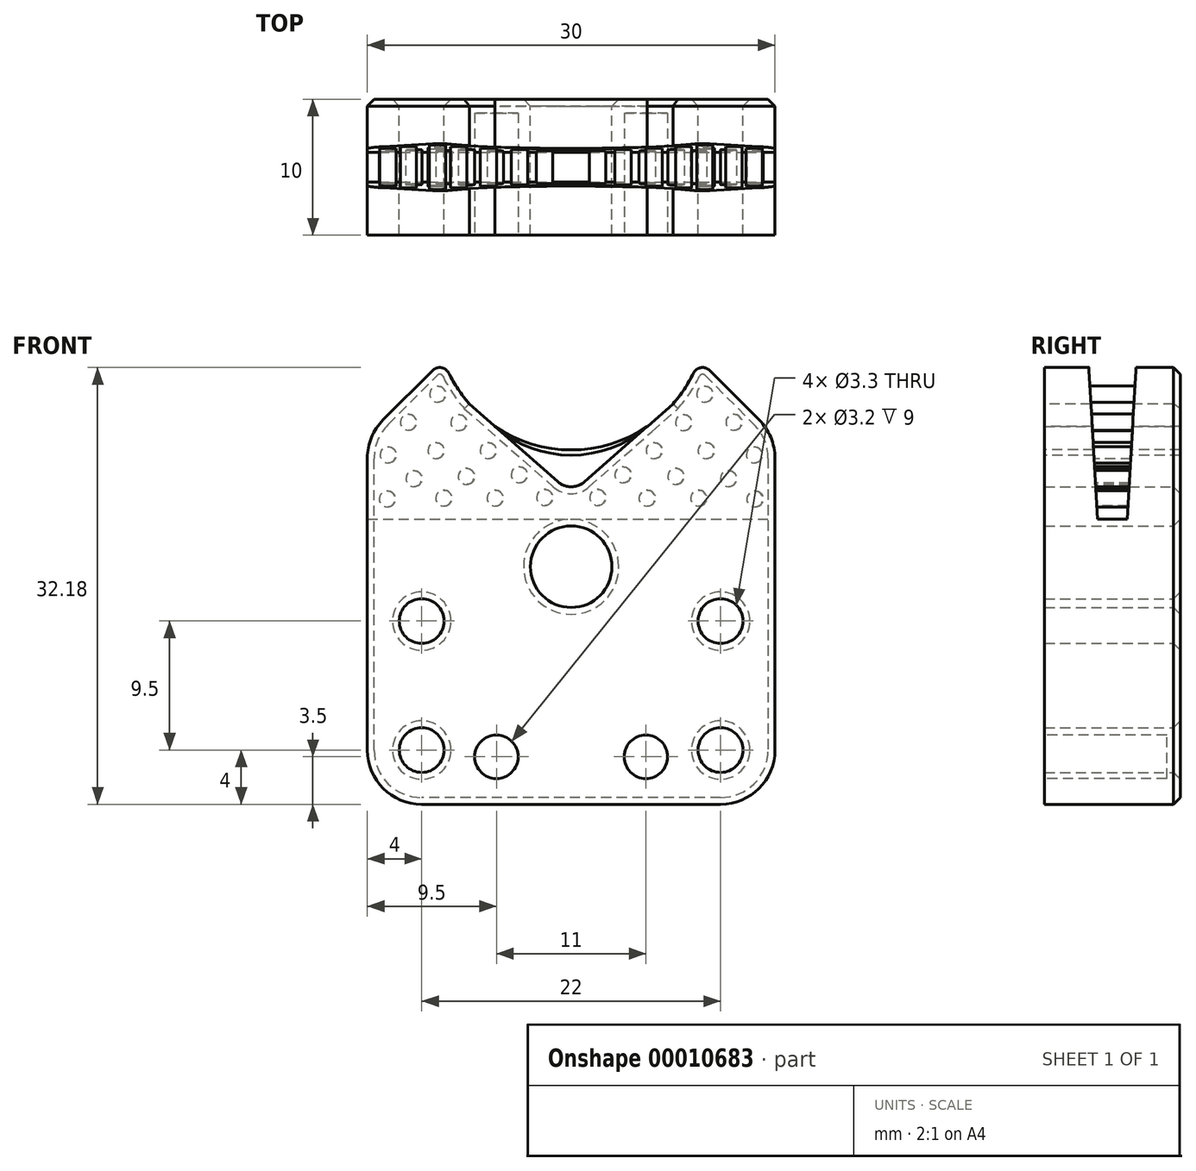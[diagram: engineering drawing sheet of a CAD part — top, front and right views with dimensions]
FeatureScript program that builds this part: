
annotation { "Feature Type Name" : "Feature", "Feature Type Description" : "" }
export const myFeature = defineFeature(function(context is Context, id is Id, definition is map)
    precondition{}
    {
        {
            var Q0;
            Q0=qCreatedBy(makeId("Front.planeOp"),FACE);
            var sketch = newSketch(context, id + "F0", { "sketchPlane" : qUnion([Q0])});
            skLineSegment(sketch, "E0.rect.bottom", {"start": v(15, -19.5) * mm, "end": v(-15, -19.5) * mm});
            skLineSegment(sketch, "E0.rect.top", {"start": v(15, 10) * mm, "end": v(-15, 10) * mm});
            skLineSegment(sketch, "E0.rect.left", {"start": v(15, -19.5) * mm, "end": v(15, 10) * mm});
            skLineSegment(sketch, "E0.rect.right", {"start": v(-15, -19.5) * mm, "end": v(-15, 10) * mm});
            skPoint(sketch, "E0.rect.middle", {"position": v(0, 0) * mm});
            skCircle(sketch, "E1", {"center": v(0, -2) * mm, "radius": 3 * mm});
            skCircle(sketch, "E2", {"center": v(-11, -6) * mm, "radius": 1.65 * mm});
            skCircle(sketch, "E3", {"center": v(11, -6) * mm, "radius": 1.65 * mm});
            skCircle(sketch, "E4", {"center": v(-11, -15.5) * mm, "radius": 1.65 * mm});
            skCircle(sketch, "E5", {"center": v(11, -15.5) * mm, "radius": 1.65 * mm});
            skSolve(sketch);
        }
        {
            var Q0;
            Q0=makeQuery(id+"F0.imprint","IMPRINT",FACE,{"disambiguationData":[TD([[makeQuery(id+"F0.imprint","IMPRINT",EDGE,{"derivedFrom":sQuery(id+"F0.wireOp",EDGE,"E0.rect.bottom")}),-1.0]])]});
            extrude(context, id + "F1", {"entities" : qUnion([Q0]), "depth" : 10 * mm});
        }
        {
            var Q0;
            Q0=makeQuery(id+"F1.opExtrude","SWEPT_EDGE",EDGE,{"disambiguationData":[OSD([sQuery(id+"F0.wireOp",EDGE,"E0.rect.top"),sQuery(id+"F0.wireOp",EDGE,"E0.rect.left")])]});
            var Q1;
            Q1=makeQuery(id+"F1.opExtrude","SWEPT_EDGE",EDGE,{"disambiguationData":[OSD([sQuery(id+"F0.wireOp",EDGE,"E0.rect.bottom"),sQuery(id+"F0.wireOp",EDGE,"E0.rect.left")])]});
            var Q2;
            Q2=makeQuery(id+"F1.opExtrude","SWEPT_EDGE",EDGE,{"disambiguationData":[OSD([sQuery(id+"F0.wireOp",EDGE,"E0.rect.top"),sQuery(id+"F0.wireOp",EDGE,"E0.rect.right")])]});
            var Q3;
            Q3=makeQuery(id+"F1.opExtrude","SWEPT_EDGE",EDGE,{"disambiguationData":[OSD([sQuery(id+"F0.wireOp",EDGE,"E0.rect.bottom"),sQuery(id+"F0.wireOp",EDGE,"E0.rect.right")])]});
            fillet(context, id + "F2", {"entities" : qUnion([Q0, Q1, Q2, Q3]), "radius" : 4 * mm, "tangentPropagation" : true, "allowEdgeOverflow" : false});
        }
        {
            var Q0;
            Q0=makeQuery(id+"F1.opExtrude","CAP_FACE",FACE,{"disambiguationData":[OSD([sQuery(id+"F0.wireOp",EDGE,"E0.rect.bottom"),sQuery(id+"F0.wireOp",EDGE,"E0.rect.top"),sQuery(id+"F0.wireOp",EDGE,"E0.rect.left"),sQuery(id+"F0.wireOp",EDGE,"E0.rect.right"),sQuery(id+"F0.wireOp",EDGE,"E1"),sQuery(id+"F0.wireOp",EDGE,"E2"),sQuery(id+"F0.wireOp",EDGE,"E3")])],"isStart":false});
            var sketch = newSketch(context, id + "F3", { "sketchPlane" : qUnion([Q0])});
            skLineSegment(sketch, "E6", {"start": v(-7.5, 10) * mm, "end": v(0, 3.39) * mm});
            skLineSegment(sketch, "E7", {"start": v(0, 3.39) * mm, "end": v(7.5, 10) * mm});
            skLineSegment(sketch, "E8", {"start": v(7.5, 10) * mm, "end": v(-7.5, 10) * mm});
            skCircle(sketch, "E9", {"center": v(0, 7.39) * mm, "radius": 3 * mm});
            skCircle(sketch, "E10", {"center": v(0, 14.72) * mm, "radius": 8.5 * mm});
            skCircle(sketch, "E11", {"center": v(0, 16.6) * mm, "radius": 9.99 * mm});
            skLineSegment(sketch, "E12", {"start": v(-13.83, 8.83) * mm, "end": v(-9.4, 13.25) * mm});
            skLineSegment(sketch, "E13", {"start": v(13.83, 8.83) * mm, "end": v(9.4, 13.25) * mm});
            skSolve(sketch);
        }
        {
            var Q0;
            {var subQ1=sQuery(id+"F3.wireOp",EDGE,"E7");var subQ3=sQuery(id+"F3.wireOp",EDGE,"E6");var subQ5=makeQuery(id+"F3.imprint","INTERSECT",VERTEX,{"derivedFrom":[subQ3,subQ1]});Q0=makeQuery(id+"F3.imprint","IMPRINT",FACE,{"disambiguationData":[TD([[makeQuery(id+"F3.imprint","IMPRINT",EDGE,{"disambiguationData":[TD([[subQ5,1.0]])],"derivedFrom":subQ3}),1.0]])]});}
            var Q1;
            {var subQ1=sQuery(id+"F3.wireOp",EDGE,"E9");var subQ5=makeQuery(id+"F3.imprint","INTERSECT",VERTEX,{"derivedFrom":[sQuery(id+"F3.wireOp",EDGE,"E6"),subQ1]});Q1=makeQuery(id+"F3.imprint","IMPRINT",FACE,{"disambiguationData":[TD([[makeQuery(id+"F3.imprint","IMPRINT",EDGE,{"disambiguationData":[TD([[subQ5,1.0]])],"derivedFrom":subQ1}),1.0]])]});}
            var Q2;
            {var subQ0=sQuery(id+"F3.wireOp",EDGE,"E10");var subQ3=sQuery(id+"F3.wireOp",EDGE,"E6");var subQ4=makeQuery(id+"F3.imprint","INTERSECT",VERTEX,{"derivedFrom":[subQ3,subQ0]});Q2=makeQuery(id+"F3.imprint","IMPRINT",FACE,{"disambiguationData":[TD([[makeQuery(id+"F3.imprint","IMPRINT",EDGE,{"disambiguationData":[TD([[subQ4,-1.0]])],"derivedFrom":subQ3}),1.0]])]});}
            var Q3;
            {var subQ0=sQuery(id+"F3.wireOp",EDGE,"E10");var subQ4=sQuery(id+"F3.wireOp",EDGE,"E8");var subQ5=makeQuery(id+"F3.imprint","INTERSECT",VERTEX,{"disambiguationData":[OD(1.0)],"derivedFrom":[subQ4,subQ0]});Q3=makeQuery(id+"F3.imprint","IMPRINT",FACE,{"disambiguationData":[TD([[makeQuery(id+"F3.imprint","IMPRINT",EDGE,{"disambiguationData":[TD([[subQ5,1.0]])],"derivedFrom":subQ4}),1.0]])]});}
            var Q4;
            {var subQ0=sQuery(id+"F3.wireOp",EDGE,"E10");var subQ3=sQuery(id+"F3.wireOp",EDGE,"E8");var subQ4=makeQuery(id+"F3.imprint","INTERSECT",VERTEX,{"disambiguationData":[OD(1.0)],"derivedFrom":[subQ3,subQ0]});Q4=makeQuery(id+"F3.imprint","IMPRINT",FACE,{"disambiguationData":[TD([[makeQuery(id+"F3.imprint","IMPRINT",EDGE,{"disambiguationData":[TD([[subQ4,-1.0]])],"derivedFrom":subQ0}),-1.0]])]});}
            var Q5;
            {var subQ0=sQuery(id+"F3.wireOp",EDGE,"E9");var subQ3=sQuery(id+"F3.wireOp",EDGE,"E8");var subQ4=makeQuery(id+"F3.imprint","INTERSECT",VERTEX,{"disambiguationData":[OD(0.0)],"derivedFrom":[subQ3,subQ0]});Q5=makeQuery(id+"F3.imprint","IMPRINT",FACE,{"disambiguationData":[TD([[makeQuery(id+"F3.imprint","IMPRINT",EDGE,{"disambiguationData":[TD([[subQ4,-1.0]])],"derivedFrom":subQ3}),1.0]])]});}
            var Q6;
            {var subQ0=sQuery(id+"F3.wireOp",EDGE,"E10");var subQ2=sQuery(id+"F3.wireOp",EDGE,"E8");var subQ3=makeQuery(id+"F3.imprint","INTERSECT",VERTEX,{"disambiguationData":[OD(0.0)],"derivedFrom":[subQ2,subQ0]});Q6=makeQuery(id+"F3.imprint","IMPRINT",FACE,{"disambiguationData":[TD([[makeQuery(id+"F3.imprint","IMPRINT",EDGE,{"disambiguationData":[TD([[subQ3,-1.0]])],"derivedFrom":subQ2}),1.0]])]});}
            var Q7;
            {var subQ1=sQuery(id+"F3.wireOp",EDGE,"E9");var subQ3=sQuery(id+"F3.wireOp",EDGE,"E7");var subQ5=makeQuery(id+"F3.imprint","INTERSECT",VERTEX,{"derivedFrom":[subQ3,subQ1]});Q7=makeQuery(id+"F3.imprint","IMPRINT",FACE,{"disambiguationData":[TD([[makeQuery(id+"F3.imprint","IMPRINT",EDGE,{"disambiguationData":[TD([[subQ5,-1.0]])],"derivedFrom":subQ3}),1.0]])]});}
            var Q8;
            {var subQ0=sQuery(id+"F3.wireOp",EDGE,"E10");var subQ3=sQuery(id+"F3.wireOp",EDGE,"E8");var subQ4=makeQuery(id+"F3.imprint","INTERSECT",VERTEX,{"disambiguationData":[OD(0.0)],"derivedFrom":[subQ3,subQ0]});Q8=makeQuery(id+"F3.imprint","IMPRINT",FACE,{"disambiguationData":[TD([[makeQuery(id+"F3.imprint","IMPRINT",EDGE,{"disambiguationData":[TD([[subQ4,1.0]])],"derivedFrom":subQ0}),-1.0]])]});}
            var Q9;
            {var subQ0=sQuery(id+"F3.wireOp",EDGE,"E11");var subQ1=sQuery(id+"F3.wireOp",EDGE,"E9");var subQ3=makeQuery(id+"F3.imprint","INTERSECT",VERTEX,{"disambiguationData":[OD(0.0)],"derivedFrom":[subQ1,subQ0]});Q9=makeQuery(id+"F3.imprint","IMPRINT",FACE,{"disambiguationData":[TD([[makeQuery(id+"F3.imprint","IMPRINT",EDGE,{"disambiguationData":[TD([[subQ3,-1.0]])],"derivedFrom":subQ1}),1.0]])]});}
            var Q10;
            {var subQ1=sQuery(id+"F3.wireOp",EDGE,"E10");var subQ3=sQuery(id+"F3.wireOp",EDGE,"E9");var subQ5=makeQuery(id+"F3.imprint","INTERSECT",VERTEX,{"disambiguationData":[OD(1.0)],"derivedFrom":[subQ3,subQ1]});Q10=makeQuery(id+"F3.imprint","IMPRINT",FACE,{"disambiguationData":[TD([[makeQuery(id+"F3.imprint","IMPRINT",EDGE,{"disambiguationData":[TD([[subQ5,-1.0]])],"derivedFrom":subQ3}),-1.0]])]});}
            var Q11;
            {var subQ0=sQuery(id+"F3.wireOp",EDGE,"E11");var subQ3=sQuery(id+"F3.wireOp",EDGE,"E9");var subQ4=makeQuery(id+"F3.imprint","INTERSECT",VERTEX,{"disambiguationData":[OD(0.0)],"derivedFrom":[subQ3,subQ0]});Q11=makeQuery(id+"F3.imprint","IMPRINT",FACE,{"disambiguationData":[TD([[makeQuery(id+"F3.imprint","IMPRINT",EDGE,{"disambiguationData":[TD([[subQ4,-1.0]])],"derivedFrom":subQ3}),-1.0]])]});}
            var Q12;
            {var subQ0=sQuery(id+"F3.wireOp",EDGE,"E11");var subQ3=sQuery(id+"F3.wireOp",EDGE,"E6");var subQ4=makeQuery(id+"F3.imprint","INTERSECT",VERTEX,{"derivedFrom":[subQ3,subQ0]});Q12=makeQuery(id+"F3.imprint","IMPRINT",FACE,{"disambiguationData":[TD([[makeQuery(id+"F3.imprint","IMPRINT",EDGE,{"disambiguationData":[TD([[subQ4,-1.0]])],"derivedFrom":subQ3}),1.0]])]});}
            extrude(context, id + "F4", {"entities" : qUnion([Q0, Q1, Q2, Q3, Q4, Q5, Q6, Q7, Q8, Q9, Q10, Q11, Q12]), "operationType" : NewBodyOperationType.REMOVE, "oppositeDirection" : true, "depth" : 10 * mm});
        }
        {
            var Q0;
            Q0=makeQuery(id+"F4.boolean.opBoolean","COPY",EDGE,{"derivedFrom":makeQuery(id+"F4.opExtrude","SWEPT_EDGE",EDGE,{"disambiguationData":[OSD([sQuery(id+"F3.wireOp",EDGE,"E6"),sQuery(id+"F3.wireOp",EDGE,"E7")])]})});
            fillet(context, id + "F5", {"entities" : qUnion([Q0]), "radius" : 1.5 * mm, "tangentPropagation" : true, "allowEdgeOverflow" : false});
        }
        {
            var Q0;
            {var subQ7=sQuery(id+"F3.wireOp",EDGE,"E12");Q0=makeQuery(id+"F3.imprint","IMPRINT",FACE,{"disambiguationData":[TD([[makeQuery(id+"F3.imprint","IMPRINT",EDGE,{"derivedFrom":subQ7}),-1.0]])]});}
            var Q1;
            {var subQ7=sQuery(id+"F3.wireOp",EDGE,"E13");Q1=makeQuery(id+"F3.imprint","IMPRINT",FACE,{"disambiguationData":[TD([[makeQuery(id+"F3.imprint","IMPRINT",EDGE,{"derivedFrom":subQ7}),1.0]])]});}
            extrude(context, id + "F6", {"entities" : qUnion([Q0, Q1]), "operationType" : NewBodyOperationType.ADD, "oppositeDirection" : true, "depth" : 10 * mm});
        }
        {
            var Q0;
            Q0=makeQuery(id+"F6.opExtrude","SWEPT_EDGE",EDGE,{"disambiguationData":[OSD([sQuery(id+"F3.wireOp",EDGE,"E11"),sQuery(id+"F3.wireOp",EDGE,"E12")])]});
            var Q1;
            Q1=makeQuery(id+"F6.opExtrude","SWEPT_EDGE",EDGE,{"disambiguationData":[OSD([sQuery(id+"F3.wireOp",EDGE,"E11"),sQuery(id+"F3.wireOp",EDGE,"E13")])]});
            fillet(context, id + "F7", {"entities" : qUnion([Q0, Q1]), "radius" : 0.75 * mm, "tangentPropagation" : true, "allowEdgeOverflow" : false});
        }
        {
            var Q0;
            Q0=makeQuery(id+"F1.opExtrude","SWEPT_FACE",FACE,{"disambiguationData":[OSD([sQuery(id+"F0.wireOp",EDGE,"E0.rect.left")])]});
            var sketch = newSketch(context, id + "F8", { "sketchPlane" : qUnion([Q0])});
            skLineSegment(sketch, "E14", {"start": v(-6.1, 1.5) * mm, "end": v(-6.75, 13) * mm});
            skLineSegment(sketch, "E15", {"start": v(-6.75, 13) * mm, "end": v(-3.25, 13) * mm});
            skLineSegment(sketch, "E16", {"start": v(-3.25, 13) * mm, "end": v(-3.9, 1.5) * mm});
            skLineSegment(sketch, "E17", {"start": v(-3.9, 1.5) * mm, "end": v(-6.1, 1.5) * mm});
            skSolve(sketch);
        }
        {
            var Q0;
            Q0=qSketchRegion(id+"F8",true);
            extrude(context, id + "F9", {"entities" : qUnion([Q0]), "operationType" : NewBodyOperationType.REMOVE, "oppositeDirection" : true, "depth" : 35 * mm});
        }
        {
            var Q0;
            {var subQ0=sQuery(id+"F0.wireOp",EDGE,"E0.rect.bottom");var subQ1=sQuery(id+"F0.wireOp",EDGE,"E0.rect.top");var subQ2=sQuery(id+"F0.wireOp",EDGE,"E0.rect.left");var subQ3=sQuery(id+"F0.wireOp",EDGE,"E0.rect.right");var subQ4=sQuery(id+"F0.wireOp",EDGE,"E1");var subQ5=sQuery(id+"F0.wireOp",EDGE,"E2");var subQ6=sQuery(id+"F0.wireOp",EDGE,"E3");var subQ7=sQuery(id+"F3.wireOp",EDGE,"E11");Q0=makeQuery(id+"F6.boolean.opBoolean","MERGE",FACE,{"derivedFrom":[makeQuery(id+"F1.opExtrude","CAP_FACE",FACE,{"disambiguationData":[OSD([subQ0,subQ1,subQ2,subQ3,subQ4,subQ5,subQ6])],"isStart":false}),makeQuery(id+"F6.opExtrude","CAP_FACE",FACE,{"disambiguationData":[OSD([subQ0,subQ1,subQ2,subQ3,subQ4,subQ5,subQ6,subQ7,sQuery(id+"F3.wireOp",EDGE,"E12")])],"isStart":true}),makeQuery(id+"F6.opExtrude","CAP_FACE",FACE,{"disambiguationData":[OSD([subQ0,subQ1,subQ2,subQ3,subQ4,subQ5,subQ6,subQ7,sQuery(id+"F3.wireOp",EDGE,"E13")])],"isStart":true})]});}
            var sketch = newSketch(context, id + "F10", { "sketchPlane" : qUnion([Q0])});
            skCircle(sketch, "E18", {"center": v(-9.83, 10.71) * mm, "radius": 0.6 * mm});
            skCircle(sketch, "E19", {"center": v(-11.98, 8.64) * mm, "radius": 0.6 * mm});
            skCircle(sketch, "E20", {"center": v(-8.28, 8.61) * mm, "radius": 0.6 * mm});
            skCircle(sketch, "E21", {"center": v(-13.47, 6.24) * mm, "radius": 0.6 * mm});
            skCircle(sketch, "E22", {"center": v(-9.94, 6.55) * mm, "radius": 0.6 * mm});
            skCircle(sketch, "E23", {"center": v(-6.1, 6.55) * mm, "radius": 0.6 * mm});
            skCircle(sketch, "E24", {"center": v(-11.58, 4.49) * mm, "radius": 0.6 * mm});
            skCircle(sketch, "E25", {"center": v(-7.71, 4.66) * mm, "radius": 0.6 * mm});
            skCircle(sketch, "E26", {"center": v(-3.81, 4.77) * mm, "radius": 0.6 * mm});
            skCircle(sketch, "E27", {"center": v(-13.53, 3) * mm, "radius": 0.6 * mm});
            skCircle(sketch, "E28", {"center": v(-9.38, 3.05) * mm, "radius": 0.6 * mm});
            skCircle(sketch, "E29", {"center": v(-5.6, 3.05) * mm, "radius": 0.6 * mm});
            skCircle(sketch, "E30", {"center": v(-1.95, 3.1) * mm, "radius": 0.6 * mm});
            skLineSegment(sketch, "E31", {"start": v(0, 0) * mm, "end": v(0, 13.84) * mm});
            skCircle(sketch, "E32.0.MirrorC", {"center": v(9.38, 3.05) * mm, "radius": 0.6 * mm});
            skCircle(sketch, "E32.1.MirrorC", {"center": v(9.83, 10.71) * mm, "radius": 0.6 * mm});
            skCircle(sketch, "E32.2.MirrorC", {"center": v(13.53, 3) * mm, "radius": 0.6 * mm});
            skCircle(sketch, "E32.3.MirrorC", {"center": v(8.28, 8.61) * mm, "radius": 0.6 * mm});
            skCircle(sketch, "E32.4.MirrorC", {"center": v(11.98, 8.64) * mm, "radius": 0.6 * mm});
            skCircle(sketch, "E32.5.MirrorC", {"center": v(1.95, 3.1) * mm, "radius": 0.6 * mm});
            skCircle(sketch, "E32.6.MirrorC", {"center": v(11.58, 4.49) * mm, "radius": 0.6 * mm});
            skCircle(sketch, "E32.7.MirrorC", {"center": v(9.94, 6.55) * mm, "radius": 0.6 * mm});
            skCircle(sketch, "E32.8.MirrorC", {"center": v(3.81, 4.77) * mm, "radius": 0.6 * mm});
            skCircle(sketch, "E32.9.MirrorC", {"center": v(5.6, 3.05) * mm, "radius": 0.6 * mm});
            skCircle(sketch, "E32.10.MirrorC", {"center": v(6.1, 6.55) * mm, "radius": 0.6 * mm});
            skCircle(sketch, "E32.11.MirrorC", {"center": v(13.47, 6.24) * mm, "radius": 0.6 * mm});
            skCircle(sketch, "E32.12.MirrorC", {"center": v(7.71, 4.66) * mm, "radius": 0.6 * mm});
            skSolve(sketch);
        }
        {
            var Q0;
            Q0=qSketchRegion(id+"F10",true);
            extrude(context, id + "F11", {"entities" : qUnion([Q0]), "operationType" : NewBodyOperationType.ADD, "oppositeDirection" : true, "depth" : 8 * mm});
        }
        {
            var Q0;
            {var subQ0=sQuery(id+"F0.wireOp",EDGE,"E0.rect.bottom");var subQ1=sQuery(id+"F0.wireOp",EDGE,"E0.rect.top");var subQ2=sQuery(id+"F0.wireOp",EDGE,"E0.rect.left");var subQ3=sQuery(id+"F0.wireOp",EDGE,"E0.rect.right");var subQ4=sQuery(id+"F0.wireOp",EDGE,"E1");var subQ5=sQuery(id+"F0.wireOp",EDGE,"E2");var subQ6=sQuery(id+"F0.wireOp",EDGE,"E3");var subQ7=sQuery(id+"F0.wireOp",EDGE,"E4");var subQ8=sQuery(id+"F0.wireOp",EDGE,"E5");var subQ9=sQuery(id+"F3.wireOp",EDGE,"E11");Q0=makeQuery(id+"F6.boolean.opBoolean","MERGE",FACE,{"derivedFrom":[makeQuery(id+"F1.opExtrude","CAP_FACE",FACE,{"disambiguationData":[OSD([subQ0,subQ1,subQ2,subQ3,subQ4,subQ5,subQ6,subQ7,subQ8])],"isStart":true}),makeQuery(id+"F6.opExtrude","CAP_FACE",FACE,{"disambiguationData":[OSD([subQ0,subQ1,subQ2,subQ3,subQ4,subQ5,subQ6,subQ7,subQ8,subQ9,sQuery(id+"F3.wireOp",EDGE,"E12")])],"isStart":false}),makeQuery(id+"F6.opExtrude","CAP_FACE",FACE,{"disambiguationData":[OSD([subQ0,subQ1,subQ2,subQ3,subQ4,subQ5,subQ6,subQ7,subQ8,subQ9,sQuery(id+"F3.wireOp",EDGE,"E13")])],"isStart":false})]});}
            chamfer(context, id + "F12", {"entities" : qUnion([Q0]), "width" : 0.5 * mm, "tangentPropagation" : true});
        }
        {
            var Q0;
            {var subQ0=sQuery(id+"F0.wireOp",EDGE,"E0.rect.bottom");var subQ1=sQuery(id+"F0.wireOp",EDGE,"E0.rect.top");var subQ2=sQuery(id+"F0.wireOp",EDGE,"E0.rect.left");var subQ3=sQuery(id+"F0.wireOp",EDGE,"E0.rect.right");var subQ4=sQuery(id+"F0.wireOp",EDGE,"E1");var subQ5=sQuery(id+"F0.wireOp",EDGE,"E2");var subQ6=sQuery(id+"F0.wireOp",EDGE,"E3");var subQ7=sQuery(id+"F0.wireOp",EDGE,"E4");var subQ8=sQuery(id+"F0.wireOp",EDGE,"E5");var subQ9=sQuery(id+"F3.wireOp",EDGE,"E11");Q0=makeQuery(id+"F6.boolean.opBoolean","MERGE",FACE,{"derivedFrom":[makeQuery(id+"F1.opExtrude","CAP_FACE",FACE,{"disambiguationData":[OSD([subQ0,subQ1,subQ2,subQ3,subQ4,subQ5,subQ6,subQ7,subQ8])],"isStart":false}),makeQuery(id+"F6.opExtrude","CAP_FACE",FACE,{"disambiguationData":[OSD([subQ0,subQ1,subQ2,subQ3,subQ4,subQ5,subQ6,subQ7,subQ8,subQ9,sQuery(id+"F3.wireOp",EDGE,"E12")])],"isStart":true}),makeQuery(id+"F6.opExtrude","CAP_FACE",FACE,{"disambiguationData":[OSD([subQ0,subQ1,subQ2,subQ3,subQ4,subQ5,subQ6,subQ7,subQ8,subQ9,sQuery(id+"F3.wireOp",EDGE,"E13")])],"isStart":true})]});}
            var sketch = newSketch(context, id + "F13", { "sketchPlane" : qUnion([Q0])});
            skCircle(sketch, "E33", {"center": v(-5.5, -16) * mm, "radius": 1.6 * mm});
            skCircle(sketch, "E34", {"center": v(5.5, -16) * mm, "radius": 1.6 * mm});
            skSolve(sketch);
        }
        {
            var Q0;
            Q0=makeQuery(id+"F13.imprint","IMPRINT",FACE,{"disambiguationData":[TD([[makeQuery(id+"F13.imprint","IMPRINT",EDGE,{"derivedFrom":sQuery(id+"F13.wireOp",EDGE,"E33")}),1.0]])]});
            var Q1;
            Q1=makeQuery(id+"F13.imprint","IMPRINT",FACE,{"disambiguationData":[TD([[makeQuery(id+"F13.imprint","IMPRINT",EDGE,{"derivedFrom":sQuery(id+"F13.wireOp",EDGE,"E34")}),1.0]])]});
            extrude(context, id + "F14", {"entities" : qUnion([Q0, Q1]), "operationType" : NewBodyOperationType.REMOVE, "oppositeDirection" : true, "depth" : 9 * mm});
        }
    });
